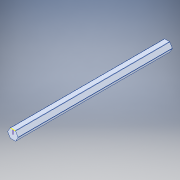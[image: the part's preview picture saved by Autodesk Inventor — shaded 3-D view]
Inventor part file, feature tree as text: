
AUTODESK INVENTOR PART (.ipt)
format: ipt  version: 2017 (Build 210142000, 142)  size: 130,048 bytes
history: native  units: in
note: dims shown in document units (in); Inventor stores cm internally (conversion verified against a paired STEP export)
features: sketch x2, split x1, fillet x1
ambient origin geometry x8: Origin, YZ Plane, XZ Plane, XY Plane, X Axis, Y Axis, Z Axis, Center Point
bodies: Solid1 (feature_tree)
feature tree (4):
  split  "Split1"
  sketch  "Sketch2"
  sketch  "Sketch1"
  fillet  "Fillet1"  Radius=8.5in
